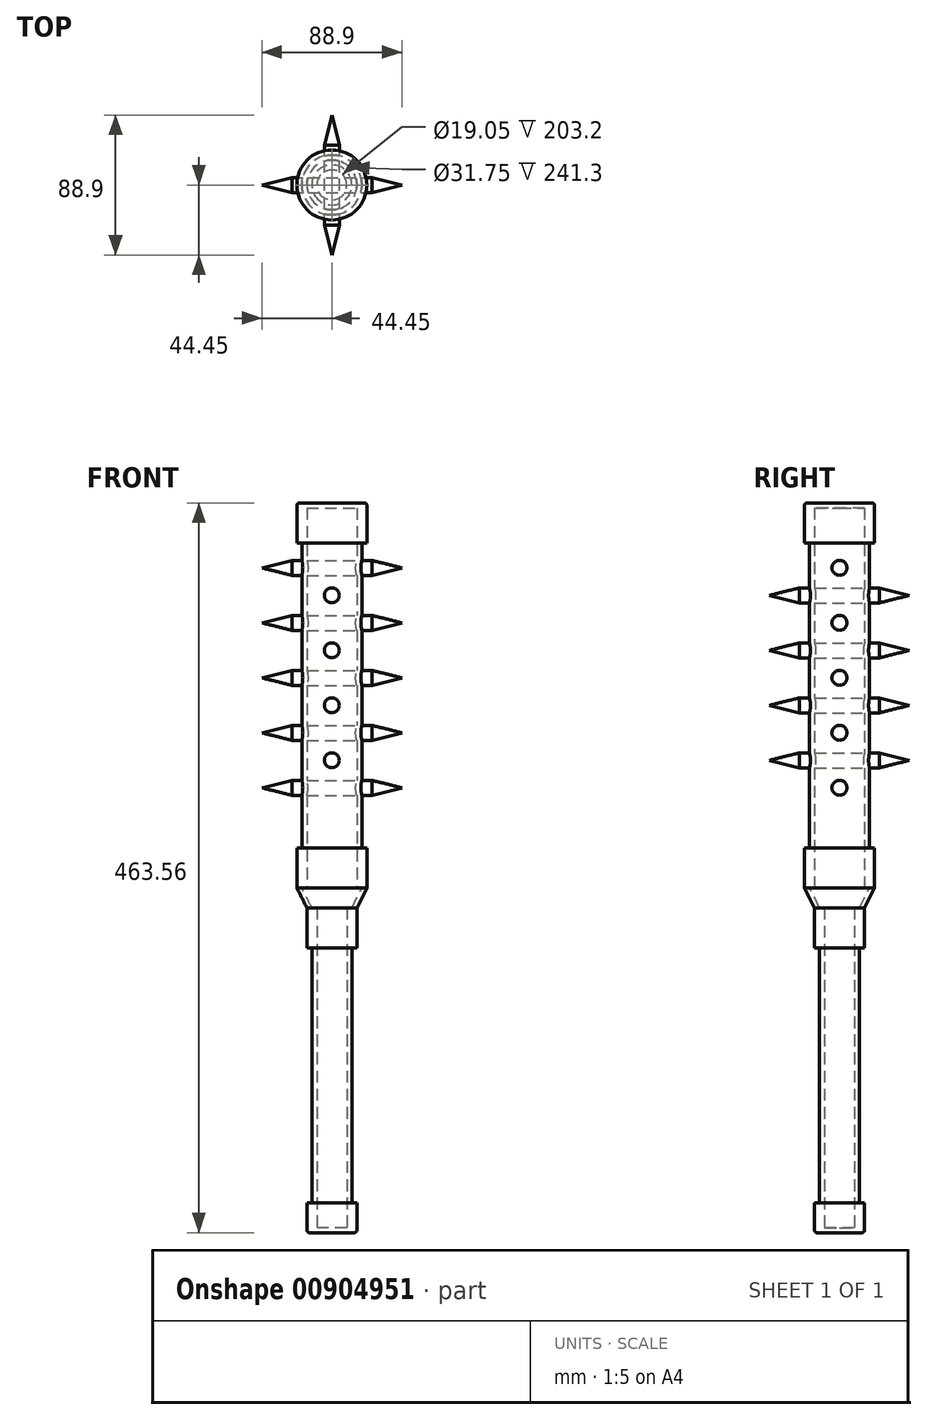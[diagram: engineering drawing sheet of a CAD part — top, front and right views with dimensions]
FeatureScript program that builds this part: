
annotation { "Feature Type Name" : "Feature", "Feature Type Description" : "" }
export const myFeature = defineFeature(function(context is Context, id is Id, definition is map)
    precondition{}
    {
        {
            var Q0;
            Q0=qCreatedBy(makeId("Top.planeOp"),FACE);
            var sketch = newSketch(context, id + "F0", { "sketchPlane" : qUnion([Q0])});
            skCircle(sketch, "E0", {"center": v(0, 0) * mm, "radius": 9.53 * mm});
            skCircle(sketch, "E1", {"center": v(0, 0) * mm, "radius": 12.7 * mm});
            skSolve(sketch);
        }
        {
            var Q0;
            Q0 = qSketchRegion(id + "F0", true);
            extrude(context, id + "F1", {"entities" : qUnion([Q0]), "depth" : 203.2 * mm, "offsetDistance" : 25.4 * mm});
        }
        {
            var Q0;
            Q0=qCreatedBy(makeId("Front.planeOp"),FACE);
            var sketch = newSketch(context, id + "F2", { "sketchPlane" : qUnion([Q0])});
            skLineSegment(sketch, "E2", {"start": v(12.7, 177.8) * mm, "end": v(12.7, 203.2) * mm});
            skLineSegment(sketch, "E3", {"start": v(12.7, 177.8) * mm, "end": v(15.87, 177.8) * mm});
            skLineSegment(sketch, "E4", {"start": v(15.87, 177.8) * mm, "end": v(15.87, 203.2) * mm});
            skLineSegment(sketch, "E5", {"start": v(15.87, 203.2) * mm, "end": v(22.22, 215.9) * mm});
            skLineSegment(sketch, "E6", {"start": v(22.22, 215.9) * mm, "end": v(22.22, 241.3) * mm});
            skLineSegment(sketch, "E7", {"start": v(22.22, 241.3) * mm, "end": v(19.05, 241.3) * mm});
            skLineSegment(sketch, "E8", {"start": v(19.05, 241.3) * mm, "end": v(19.05, 215.9) * mm});
            skLineSegment(sketch, "E9", {"start": v(19.05, 215.9) * mm, "end": v(12.7, 203.2) * mm});
            skLineSegment(sketch, "E10", {"start": v(19.05, 215.9) * mm, "end": v(15.87, 215.9) * mm});
            skLineSegment(sketch, "E11", {"start": v(15.87, 215.9) * mm, "end": v(15.87, 457.2) * mm});
            skLineSegment(sketch, "E12", {"start": v(15.87, 457.2) * mm, "end": v(19.05, 457.2) * mm});
            skLineSegment(sketch, "E13", {"start": v(19.05, 241.3) * mm, "end": v(19.05, 457.2) * mm});
            skLineSegment(sketch, "E14", {"start": v(0, 177.8) * mm, "end": v(0, 457.2) * mm, "construction": true});
            skSolve(sketch);
        }
        {
            var Q0;
            Q0=makeQuery(id+"F2.imprint","IMPRINT",FACE,{"disambiguationData":[TD([[makeQuery(id+"F2.imprint","IMPRINT",EDGE,{"derivedFrom":sQuery(id+"F2.wireOp",EDGE,"E8")}),-1.0]])]});
            var Q1;
            Q1=makeQuery(id+"F2.imprint","IMPRINT",FACE,{"disambiguationData":[TD([[makeQuery(id+"F2.imprint","IMPRINT",EDGE,{"derivedFrom":sQuery(id+"F2.wireOp",EDGE,"E2")}),-1.0]])]});
            var Q2;
            Q2=sQuery(id+"F2.wireOp",EDGE,"E14");
            revolve(context, id + "F3", {"operationType" : NewBodyOperationType.ADD, "surfaceOperationType" : NewSurfaceOperationType.NEW, "entities" : qUnion([Q0, Q1]), "axis" : qUnion([Q2]), "revolveType" : RevolveType.FULL});
        }
        {
            var Q0;
            Q0=qCreatedBy(makeId("Front.planeOp"),FACE);
            var sketch = newSketch(context, id + "F4", { "sketchPlane" : qUnion([Q0])});
            skLineSegment(sketch, "E15", {"start": v(0, 0) * mm, "end": v(0, -3.18) * mm});
            skLineSegment(sketch, "E16", {"start": v(0, -3.18) * mm, "end": v(14.29, -3.18) * mm});
            skLineSegment(sketch, "E17", {"start": v(15.88, -1.59) * mm, "end": v(15.87, 15.88) * mm});
            skLineSegment(sketch, "E18", {"start": v(15.88, 15.88) * mm, "end": v(12.7, 15.88) * mm});
            skLineSegment(sketch, "E19", {"start": v(12.7, 15.88) * mm, "end": v(12.7, 0) * mm});
            skLineSegment(sketch, "E20", {"start": v(12.7, 0) * mm, "end": v(0, 0) * mm});
            skLineSegment(sketch, "E21", {"start": v(0, 457.2) * mm, "end": v(0, 460.38) * mm});
            skLineSegment(sketch, "E22", {"start": v(0, 460.38) * mm, "end": v(20.64, 460.38) * mm});
            skLineSegment(sketch, "E23", {"start": v(22.23, 458.79) * mm, "end": v(22.23, 434.98) * mm});
            skLineSegment(sketch, "E24", {"start": v(22.23, 434.98) * mm, "end": v(19.05, 434.98) * mm});
            skLineSegment(sketch, "E25", {"start": v(19.05, 434.98) * mm, "end": v(19.05, 457.2) * mm});
            skLineSegment(sketch, "E26", {"start": v(19.05, 457.2) * mm, "end": v(0, 457.2) * mm});
            skPoint(sketch, "E27.visualSharp", {"position": v(22.23, 460.38) * mm});
            skArc(sketch, "E27.filletArc", {"start": v(22.22, 458.79) * mm, "mid": v(21.76, 459.91) * mm, "end": v(20.64, 460.38) * mm});
            skPoint(sketch, "E28.visualSharp", {"position": v(15.88, -3.18) * mm});
            skArc(sketch, "E28.filletArc", {"start": v(14.29, -3.17) * mm, "mid": v(15.41, -2.71) * mm, "end": v(15.88, -1.59) * mm});
            skSolve(sketch);
        }
        {
            var Q0;
            Q0=makeQuery(id+"F4.imprint","IMPRINT",FACE,{"disambiguationData":[TD([[makeQuery(id+"F4.imprint","IMPRINT",EDGE,{"derivedFrom":sQuery(id+"F4.wireOp",EDGE,"E21")}),-1.0]])]});
            var Q1;
            Q1=makeQuery(id+"F4.imprint","IMPRINT",FACE,{"disambiguationData":[TD([[makeQuery(id+"F4.imprint","IMPRINT",EDGE,{"derivedFrom":sQuery(id+"F4.wireOp",EDGE,"E15")}),1.0]])]});
            var Q2;
            Q2=sQuery(id+"F4.wireOp",EDGE,"E15");
            revolve(context, id + "F5", {"operationType" : NewBodyOperationType.ADD, "surfaceOperationType" : NewSurfaceOperationType.NEW, "entities" : qUnion([Q0, Q1]), "axis" : qUnion([Q2]), "revolveType" : RevolveType.FULL});
        }
        {
            var Q0;
            Q0=qCreatedBy(makeId("Front.planeOp"),FACE);
            var sketch = newSketch(context, id + "F6", { "sketchPlane" : qUnion([Q0])});
            skLineSegment(sketch, "E29.bottom", {"start": v(44.45, 414.34) * mm, "end": v(-44.45, 414.34) * mm, "construction": true});
            skLineSegment(sketch, "E29.top", {"start": v(44.45, 423.86) * mm, "end": v(-44.45, 423.86) * mm});
            skLineSegment(sketch, "E29.left", {"start": v(44.45, 414.34) * mm, "end": v(44.45, 423.86) * mm, "construction": true});
            skLineSegment(sketch, "E29.right", {"start": v(-44.45, 414.34) * mm, "end": v(-44.45, 423.86) * mm, "construction": true});
            skPoint(sketch, "E29.middle", {"position": v(0, 419.1) * mm});
            skLineSegment(sketch, "E30", {"start": v(44.45, 419.1) * mm, "end": v(-44.45, 419.1) * mm});
            skLineSegment(sketch, "E31", {"start": v(-44.45, 419.1) * mm, "end": v(-25.4, 423.86) * mm});
            skLineSegment(sketch, "E32", {"start": v(44.45, 419.1) * mm, "end": v(25.4, 423.86) * mm});
            skLineSegment(sketch, "E33.bottom", {"start": v(44.45, 388.94) * mm, "end": v(-44.45, 388.94) * mm});
            skLineSegment(sketch, "E33.top", {"start": v(44.45, 379.41) * mm, "end": v(-44.45, 379.41) * mm, "construction": true});
            skLineSegment(sketch, "E33.left", {"start": v(44.45, 388.94) * mm, "end": v(44.45, 379.41) * mm, "construction": true});
            skLineSegment(sketch, "E33.right", {"start": v(-44.45, 388.94) * mm, "end": v(-44.45, 379.41) * mm, "construction": true});
            skPoint(sketch, "E33.middle", {"position": v(0, 384.18) * mm});
            skPoint(sketch, "E33.middle.positionSnap0", {"position": v(0, 423.86) * mm});
            skPoint(sketch, "E33.centerSnap0", {"position": v(0, 423.86) * mm});
            skLineSegment(sketch, "E34", {"start": v(44.45, 384.18) * mm, "end": v(-44.45, 384.18) * mm});
            skLineSegment(sketch, "E35", {"start": v(-44.45, 384.18) * mm, "end": v(-25.4, 388.94) * mm});
            skLineSegment(sketch, "E36", {"start": v(44.45, 384.18) * mm, "end": v(25.4, 388.94) * mm});
            skLineSegment(sketch, "E37.bottom", {"start": v(44.45, 344.49) * mm, "end": v(-44.45, 344.49) * mm, "construction": true});
            skLineSegment(sketch, "E37.top", {"start": v(44.45, 354.01) * mm, "end": v(-44.45, 354.01) * mm});
            skLineSegment(sketch, "E37.left", {"start": v(44.45, 344.49) * mm, "end": v(44.45, 354.01) * mm, "construction": true});
            skLineSegment(sketch, "E37.right", {"start": v(-44.45, 344.49) * mm, "end": v(-44.45, 354.01) * mm, "construction": true});
            skPoint(sketch, "E37.middle", {"position": v(0, 349.25) * mm});
            skLineSegment(sketch, "E38", {"start": v(44.45, 349.25) * mm, "end": v(-44.45, 349.25) * mm});
            skLineSegment(sketch, "E39", {"start": v(-44.45, 349.25) * mm, "end": v(-25.4, 354.01) * mm});
            skLineSegment(sketch, "E40", {"start": v(44.45, 349.25) * mm, "end": v(25.4, 354.01) * mm});
            skLineSegment(sketch, "E41.bottom", {"start": v(44.45, 319.09) * mm, "end": v(-44.45, 319.09) * mm});
            skLineSegment(sketch, "E41.top", {"start": v(44.45, 309.56) * mm, "end": v(-44.45, 309.56) * mm, "construction": true});
            skLineSegment(sketch, "E41.left", {"start": v(44.45, 319.09) * mm, "end": v(44.45, 309.56) * mm, "construction": true});
            skLineSegment(sketch, "E41.right", {"start": v(-44.45, 319.09) * mm, "end": v(-44.45, 309.56) * mm, "construction": true});
            skPoint(sketch, "E41.middle", {"position": v(0, 314.33) * mm});
            skPoint(sketch, "E41.middle.positionSnap0", {"position": v(0, 354.01) * mm});
            skPoint(sketch, "E41.centerSnap0", {"position": v(0, 354.01) * mm});
            skLineSegment(sketch, "E42", {"start": v(44.45, 314.33) * mm, "end": v(-44.45, 314.33) * mm});
            skLineSegment(sketch, "E43", {"start": v(-44.45, 314.33) * mm, "end": v(-25.4, 319.09) * mm});
            skLineSegment(sketch, "E44", {"start": v(44.45, 314.33) * mm, "end": v(25.4, 319.09) * mm});
            skLineSegment(sketch, "E45.left", {"start": v(44.45, 379.41) * mm, "end": v(44.45, 388.94) * mm, "construction": true});
            skLineSegment(sketch, "E45.right", {"start": v(-44.45, 379.41) * mm, "end": v(-44.45, 388.94) * mm, "construction": true});
            skLineSegment(sketch, "E46.left", {"start": v(44.45, 354.01) * mm, "end": v(44.45, 344.49) * mm, "construction": true});
            skLineSegment(sketch, "E46.right", {"start": v(-44.45, 354.01) * mm, "end": v(-44.45, 344.49) * mm, "construction": true});
            skPoint(sketch, "E46.middle.positionSnap0", {"position": v(0, 388.94) * mm});
            skPoint(sketch, "E46.centerSnap0", {"position": v(0, 388.94) * mm});
            skLineSegment(sketch, "E47.left", {"start": v(44.45, 314.33) * mm, "end": v(44.45, 319.09) * mm, "construction": true});
            skLineSegment(sketch, "E47.right", {"start": v(-44.45, 309.56) * mm, "end": v(-44.45, 319.09) * mm, "construction": true});
            skLineSegment(sketch, "E48.bottom", {"start": v(44.45, 284.16) * mm, "end": v(-44.45, 284.16) * mm});
            skLineSegment(sketch, "E48.top", {"start": v(44.45, 274.64) * mm, "end": v(-44.45, 274.64) * mm, "construction": true});
            skLineSegment(sketch, "E48.left", {"start": v(44.45, 284.16) * mm, "end": v(44.45, 274.64) * mm, "construction": true});
            skLineSegment(sketch, "E48.right", {"start": v(-44.45, 284.16) * mm, "end": v(-44.45, 274.64) * mm, "construction": true});
            skPoint(sketch, "E48.middle", {"position": v(0, 279.4) * mm});
            skPoint(sketch, "E48.middle.positionSnap0", {"position": v(0, 319.09) * mm});
            skPoint(sketch, "E48.centerSnap0", {"position": v(0, 319.09) * mm});
            skLineSegment(sketch, "E49", {"start": v(44.45, 279.4) * mm, "end": v(-44.45, 279.4) * mm});
            skLineSegment(sketch, "E50", {"start": v(-44.45, 279.4) * mm, "end": v(-25.4, 284.16) * mm});
            skLineSegment(sketch, "E51", {"start": v(44.45, 279.4) * mm, "end": v(25.4, 284.16) * mm});
            skSolve(sketch);
        }
        {
            var Q0;
            Q0=qCreatedBy(makeId("Right.planeOp"),FACE);
            var sketch = newSketch(context, id + "F7", { "sketchPlane" : qUnion([Q0])});
            skLineSegment(sketch, "E52.bottom", {"start": v(44.45, 396.88) * mm, "end": v(-44.45, 396.88) * mm, "construction": true});
            skLineSegment(sketch, "E52.top", {"start": v(44.45, 406.4) * mm, "end": v(-44.45, 406.4) * mm});
            skLineSegment(sketch, "E52.left", {"start": v(44.45, 396.88) * mm, "end": v(44.45, 406.4) * mm, "construction": true});
            skLineSegment(sketch, "E52.right", {"start": v(-44.45, 396.88) * mm, "end": v(-44.45, 406.4) * mm, "construction": true});
            skPoint(sketch, "E52.middle", {"position": v(0, 401.64) * mm});
            skLineSegment(sketch, "E53", {"start": v(44.45, 401.64) * mm, "end": v(-44.45, 401.64) * mm});
            skLineSegment(sketch, "E54", {"start": v(-44.45, 401.64) * mm, "end": v(-25.4, 406.4) * mm});
            skLineSegment(sketch, "E55", {"start": v(44.45, 401.64) * mm, "end": v(25.4, 406.4) * mm});
            skLineSegment(sketch, "E56.bottom", {"start": v(44.45, 371.48) * mm, "end": v(-44.45, 371.48) * mm});
            skLineSegment(sketch, "E56.top", {"start": v(44.45, 361.95) * mm, "end": v(-44.45, 361.95) * mm, "construction": true});
            skLineSegment(sketch, "E56.left", {"start": v(44.45, 371.48) * mm, "end": v(44.45, 361.95) * mm, "construction": true});
            skLineSegment(sketch, "E56.right", {"start": v(-44.45, 371.48) * mm, "end": v(-44.45, 361.95) * mm, "construction": true});
            skPoint(sketch, "E56.middle", {"position": v(0, 366.71) * mm});
            skPoint(sketch, "E56.middle.positionSnap0", {"position": v(0, 406.4) * mm});
            skPoint(sketch, "E56.centerSnap0", {"position": v(0, 406.4) * mm});
            skLineSegment(sketch, "E57", {"start": v(44.45, 366.71) * mm, "end": v(-44.45, 366.71) * mm});
            skLineSegment(sketch, "E58", {"start": v(-44.45, 366.71) * mm, "end": v(-25.4, 371.48) * mm});
            skLineSegment(sketch, "E59", {"start": v(44.45, 366.71) * mm, "end": v(25.4, 371.48) * mm});
            skLineSegment(sketch, "E60.bottom", {"start": v(44.45, 327.03) * mm, "end": v(-44.45, 327.03) * mm, "construction": true});
            skLineSegment(sketch, "E60.top", {"start": v(44.45, 336.55) * mm, "end": v(-44.45, 336.55) * mm});
            skLineSegment(sketch, "E60.left", {"start": v(44.45, 327.03) * mm, "end": v(44.45, 336.55) * mm, "construction": true});
            skLineSegment(sketch, "E60.right", {"start": v(-44.45, 327.03) * mm, "end": v(-44.45, 336.55) * mm, "construction": true});
            skPoint(sketch, "E60.middle", {"position": v(0, 331.79) * mm});
            skLineSegment(sketch, "E61", {"start": v(44.45, 331.79) * mm, "end": v(-44.45, 331.79) * mm});
            skLineSegment(sketch, "E62", {"start": v(-44.45, 331.79) * mm, "end": v(-25.4, 336.55) * mm});
            skLineSegment(sketch, "E63", {"start": v(44.45, 331.79) * mm, "end": v(25.4, 336.55) * mm});
            skLineSegment(sketch, "E64.bottom", {"start": v(44.45, 301.63) * mm, "end": v(-44.45, 301.63) * mm});
            skLineSegment(sketch, "E64.top", {"start": v(44.45, 292.1) * mm, "end": v(-44.45, 292.1) * mm, "construction": true});
            skLineSegment(sketch, "E64.left", {"start": v(44.45, 301.63) * mm, "end": v(44.45, 292.1) * mm, "construction": true});
            skLineSegment(sketch, "E64.right", {"start": v(-44.45, 301.63) * mm, "end": v(-44.45, 292.1) * mm, "construction": true});
            skPoint(sketch, "E64.middle", {"position": v(0, 296.86) * mm});
            skPoint(sketch, "E64.middle.positionSnap0", {"position": v(0, 336.55) * mm});
            skPoint(sketch, "E64.centerSnap0", {"position": v(0, 336.55) * mm});
            skLineSegment(sketch, "E65", {"start": v(44.45, 296.86) * mm, "end": v(-44.45, 296.86) * mm});
            skLineSegment(sketch, "E66", {"start": v(-44.45, 296.86) * mm, "end": v(-25.4, 301.63) * mm});
            skLineSegment(sketch, "E67", {"start": v(44.45, 296.86) * mm, "end": v(25.4, 301.63) * mm});
            skSolve(sketch);
        }
        {
            var Q0;
            Q0=makeQuery(id+"F6.imprint","IMPRINT",FACE,{"disambiguationData":[TD([[makeQuery(id+"F6.imprint","IMPRINT",EDGE,{"derivedFrom":sQuery(id+"F6.wireOp",EDGE,"E30")}),-1.0]])]});
            var Q1;
            Q1=sQuery(id+"F6.wireOp",EDGE,"E30");
            revolve(context, id + "F8", {"operationType" : NewBodyOperationType.ADD, "surfaceOperationType" : NewSurfaceOperationType.NEW, "entities" : qUnion([Q0]), "axis" : qUnion([Q1]), "revolveType" : RevolveType.FULL});
        }
        {
            var Q0;
            Q0=makeQuery(id+"F6.imprint","IMPRINT",FACE,{"disambiguationData":[TD([[makeQuery(id+"F6.imprint","IMPRINT",EDGE,{"derivedFrom":sQuery(id+"F6.wireOp",EDGE,"E34")}),-1.0]])]});
            var Q1;
            Q1=sQuery(id+"F6.wireOp",EDGE,"E34");
            revolve(context, id + "F9", {"operationType" : NewBodyOperationType.ADD, "surfaceOperationType" : NewSurfaceOperationType.NEW, "entities" : qUnion([Q0]), "axis" : qUnion([Q1]), "revolveType" : RevolveType.FULL});
        }
        {
            var Q0;
            Q0=makeQuery(id+"F7.imprint","IMPRINT",FACE,{"disambiguationData":[TD([[makeQuery(id+"F7.imprint","IMPRINT",EDGE,{"derivedFrom":sQuery(id+"F7.wireOp",EDGE,"E53")}),-1.0]])]});
            var Q1;
            Q1=sQuery(id+"F7.wireOp",EDGE,"E53");
            revolve(context, id + "F10", {"operationType" : NewBodyOperationType.ADD, "surfaceOperationType" : NewSurfaceOperationType.NEW, "entities" : qUnion([Q0]), "axis" : qUnion([Q1]), "revolveType" : RevolveType.FULL});
        }
        {
            var Q0;
            Q0=makeQuery(id+"F7.imprint","IMPRINT",FACE,{"disambiguationData":[TD([[makeQuery(id+"F7.imprint","IMPRINT",EDGE,{"derivedFrom":sQuery(id+"F7.wireOp",EDGE,"E57")}),-1.0]])]});
            var Q1;
            Q1=sQuery(id+"F7.wireOp",EDGE,"E57");
            revolve(context, id + "F11", {"operationType" : NewBodyOperationType.ADD, "surfaceOperationType" : NewSurfaceOperationType.NEW, "entities" : qUnion([Q0]), "axis" : qUnion([Q1]), "revolveType" : RevolveType.FULL});
        }
        {
            var Q0;
            Q0=makeQuery(id+"F6.imprint","IMPRINT",FACE,{"disambiguationData":[TD([[makeQuery(id+"F6.imprint","IMPRINT",EDGE,{"derivedFrom":sQuery(id+"F6.wireOp",EDGE,"E38")}),-1.0]])]});
            var Q1;
            Q1=sQuery(id+"F6.wireOp",EDGE,"E38");
            revolve(context, id + "F12", {"operationType" : NewBodyOperationType.ADD, "surfaceOperationType" : NewSurfaceOperationType.NEW, "entities" : qUnion([Q0]), "axis" : qUnion([Q1]), "revolveType" : RevolveType.FULL});
        }
        {
            var Q0;
            Q0=makeQuery(id+"F6.imprint","IMPRINT",FACE,{"disambiguationData":[TD([[makeQuery(id+"F6.imprint","IMPRINT",EDGE,{"derivedFrom":sQuery(id+"F6.wireOp",EDGE,"E42")}),-1.0]])]});
            var Q1;
            Q1=sQuery(id+"F6.wireOp",EDGE,"E42");
            revolve(context, id + "F13", {"operationType" : NewBodyOperationType.ADD, "surfaceOperationType" : NewSurfaceOperationType.NEW, "entities" : qUnion([Q0]), "axis" : qUnion([Q1]), "revolveType" : RevolveType.FULL});
        }
        {
            var Q0;
            Q0=makeQuery(id+"F7.imprint","IMPRINT",FACE,{"disambiguationData":[TD([[makeQuery(id+"F7.imprint","IMPRINT",EDGE,{"derivedFrom":sQuery(id+"F7.wireOp",EDGE,"E61")}),-1.0]])]});
            var Q1;
            Q1=sQuery(id+"F7.wireOp",EDGE,"E61");
            revolve(context, id + "F14", {"operationType" : NewBodyOperationType.ADD, "surfaceOperationType" : NewSurfaceOperationType.NEW, "entities" : qUnion([Q0]), "axis" : qUnion([Q1]), "revolveType" : RevolveType.FULL});
        }
        {
            var Q0;
            Q0=makeQuery(id+"F7.imprint","IMPRINT",FACE,{"disambiguationData":[TD([[makeQuery(id+"F7.imprint","IMPRINT",EDGE,{"derivedFrom":sQuery(id+"F7.wireOp",EDGE,"E65")}),-1.0]])]});
            var Q1;
            Q1=sQuery(id+"F7.wireOp",EDGE,"E65");
            revolve(context, id + "F15", {"operationType" : NewBodyOperationType.ADD, "surfaceOperationType" : NewSurfaceOperationType.NEW, "entities" : qUnion([Q0]), "axis" : qUnion([Q1]), "revolveType" : RevolveType.FULL});
        }
        {
            var Q0;
            Q0=makeQuery(id+"F6.imprint","IMPRINT",FACE,{"disambiguationData":[TD([[makeQuery(id+"F6.imprint","IMPRINT",EDGE,{"derivedFrom":sQuery(id+"F6.wireOp",EDGE,"E49")}),-1.0]])]});
            var Q1;
            Q1=sQuery(id+"F6.wireOp",EDGE,"E49");
            revolve(context, id + "F16", {"operationType" : NewBodyOperationType.ADD, "surfaceOperationType" : NewSurfaceOperationType.NEW, "entities" : qUnion([Q0]), "axis" : qUnion([Q1]), "revolveType" : RevolveType.FULL});
        }
    });
